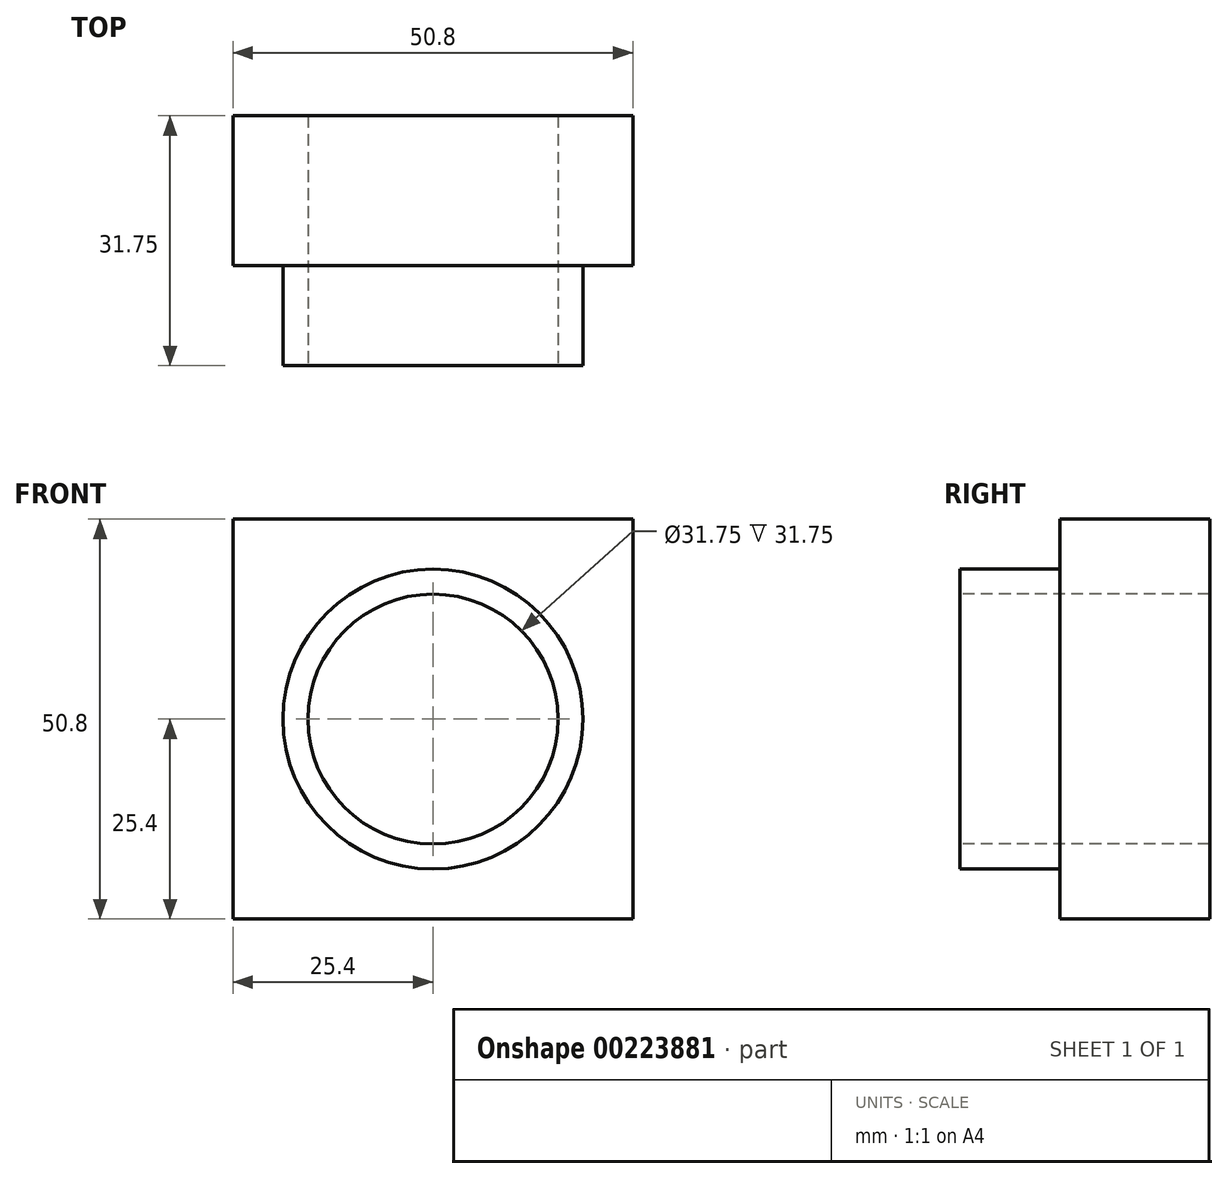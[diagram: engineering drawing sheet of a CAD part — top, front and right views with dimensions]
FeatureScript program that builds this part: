
annotation { "Feature Type Name" : "Feature", "Feature Type Description" : "" }
export const myFeature = defineFeature(function(context is Context, id is Id, definition is map)
    precondition{}
    {
        {
            var Q0;
            Q0=qCreatedBy(makeId("Front.planeOp"),FACE);
            var sketch = newSketch(context, id + "F0", { "sketchPlane" : qUnion([Q0])});
            skPoint(sketch, "E0.middle", {"position": v(0, 0) * mm});
            skLineSegment(sketch, "E1.bottom", {"start": v(25.4, 25.4) * mm, "end": v(-25.4, 25.4) * mm});
            skLineSegment(sketch, "E1.top", {"start": v(25.4, -25.4) * mm, "end": v(-25.4, -25.4) * mm});
            skLineSegment(sketch, "E1.left", {"start": v(25.4, 25.4) * mm, "end": v(25.4, -25.4) * mm});
            skLineSegment(sketch, "E1.right", {"start": v(-25.4, 25.4) * mm, "end": v(-25.4, -25.4) * mm});
            skSolve(sketch);
        }
        {
            var Q0;
            Q0 = qSketchRegion(id + "F0", true);
            extrude(context, id + "F1", {"entities" : qUnion([Q0]), "depth" : 19.05 * mm});
        }
        {
            var Q0;
            Q0=makeQuery(id+"F1.opExtrude","CAP_FACE",FACE,{"disambiguationData":[OSD([sQuery(id+"F0.wireOp",EDGE,"E1.bottom"),sQuery(id+"F0.wireOp",EDGE,"E1.top"),sQuery(id+"F0.wireOp",EDGE,"E1.left"),sQuery(id+"F0.wireOp",EDGE,"E1.right")])],"isStart":false});
            var sketch = newSketch(context, id + "F2", { "sketchPlane" : qUnion([Q0])});
            skCircle(sketch, "E2", {"center": v(0, 0) * mm, "radius": 19.05 * mm});
            skSolve(sketch);
        }
        {
            var Q0;
            Q0 = qSketchRegion(id + "F2", true);
            extrude(context, id + "F3", {"entities" : qUnion([Q0]), "operationType" : NewBodyOperationType.ADD, "depth" : 12.7 * mm});
        }
        {
            var Q0;
            Q0=makeQuery(id+"F3.opExtrude","CAP_FACE",FACE,{"disambiguationData":[OSD([sQuery(id+"F2.wireOp",EDGE,"E2")])],"isStart":false});
            var sketch = newSketch(context, id + "F4", { "sketchPlane" : qUnion([Q0])});
            skCircle(sketch, "E3", {"center": v(0, 0) * mm, "radius": 15.88 * mm});
            skSolve(sketch);
        }
        {
            var Q0;
            Q0 = qSketchRegion(id + "F4", true);
            extrude(context, id + "F5", {"entities" : qUnion([Q0]), "operationType" : NewBodyOperationType.REMOVE, "oppositeDirection" : true, "depth" : 50.3 * mm});
        }
    });
